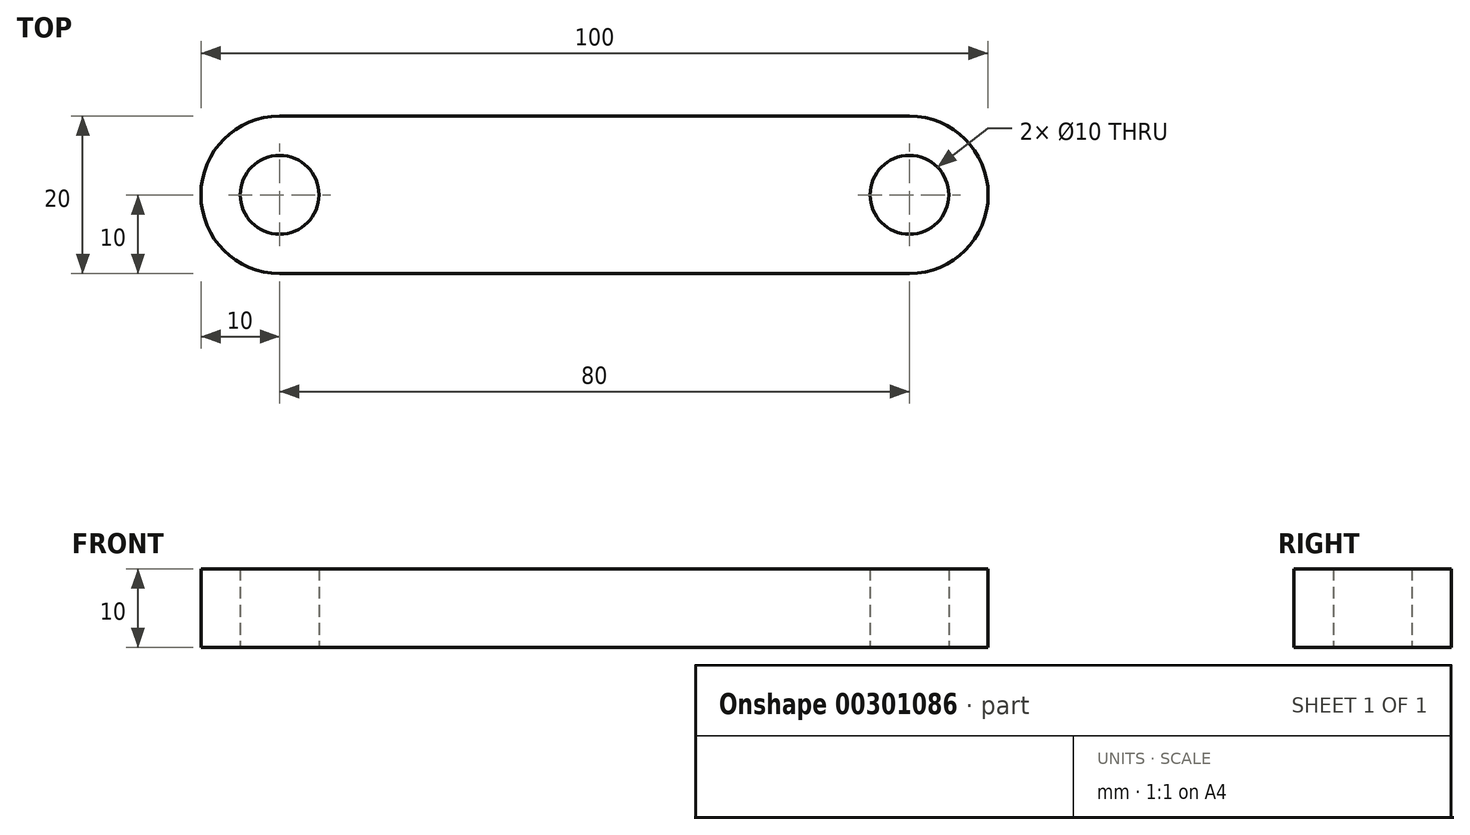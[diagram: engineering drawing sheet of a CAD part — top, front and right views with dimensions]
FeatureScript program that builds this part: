
annotation { "Feature Type Name" : "Feature", "Feature Type Description" : "" }
export const myFeature = defineFeature(function(context is Context, id is Id, definition is map)
    precondition{}
    {
        {
            var Q0;
            Q0=qCreatedBy(makeId("Top.planeOp"),FACE);
            var sketch = newSketch(context, id + "F0", { "sketchPlane" : qUnion([Q0])});
            skArc(sketch, "E0", {"start": v(0, 10) * mm, "mid": v(-10, 0) * mm, "end": v(0, -10) * mm});
            skArc(sketch, "E1", {"start": v(80, -10) * mm, "mid": v(90, 0) * mm, "end": v(80, 10) * mm});
            skLineSegment(sketch, "E2", {"start": v(0, 10) * mm, "end": v(80, 10) * mm});
            skLineSegment(sketch, "E3", {"start": v(0, -10) * mm, "end": v(80, -10) * mm});
            skCircle(sketch, "E4", {"center": v(0, 0) * mm, "radius": 5 * mm});
            skCircle(sketch, "E5", {"center": v(80, 0) * mm, "radius": 5 * mm});
            skSolve(sketch);
        }
        {
            var Q0;
            Q0=makeQuery(id+"F0.imprint","IMPRINT",FACE,{"disambiguationData":[TD([[makeQuery(id+"F0.imprint","IMPRINT",EDGE,{"derivedFrom":sQuery(id+"F0.wireOp",EDGE,"E0")}),1.0]])]});
            extrude(context, id + "F1", {"entities" : qUnion([Q0]), "depth" : 10 * mm});
        }
    });
